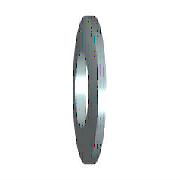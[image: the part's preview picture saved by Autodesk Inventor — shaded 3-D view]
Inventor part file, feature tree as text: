
AUTODESK INVENTOR PART (.ipt)
format: ipt  version: 2017 (Build 210142000, 142)  size: 117,248 bytes
history: native  units: mm (DEFAULTED — no unit token found)
features: other x2, plane x1
ambient origin geometry x7: Origin, YZ Plane, XY Plane, X Axis, Y Axis, Z Axis, Center Point
bodies: Solid1 (feature_tree)
feature tree (3):
  other  "IDS_BODY"
  other  "Work Axis1"
  plane  "Work Plane1"
